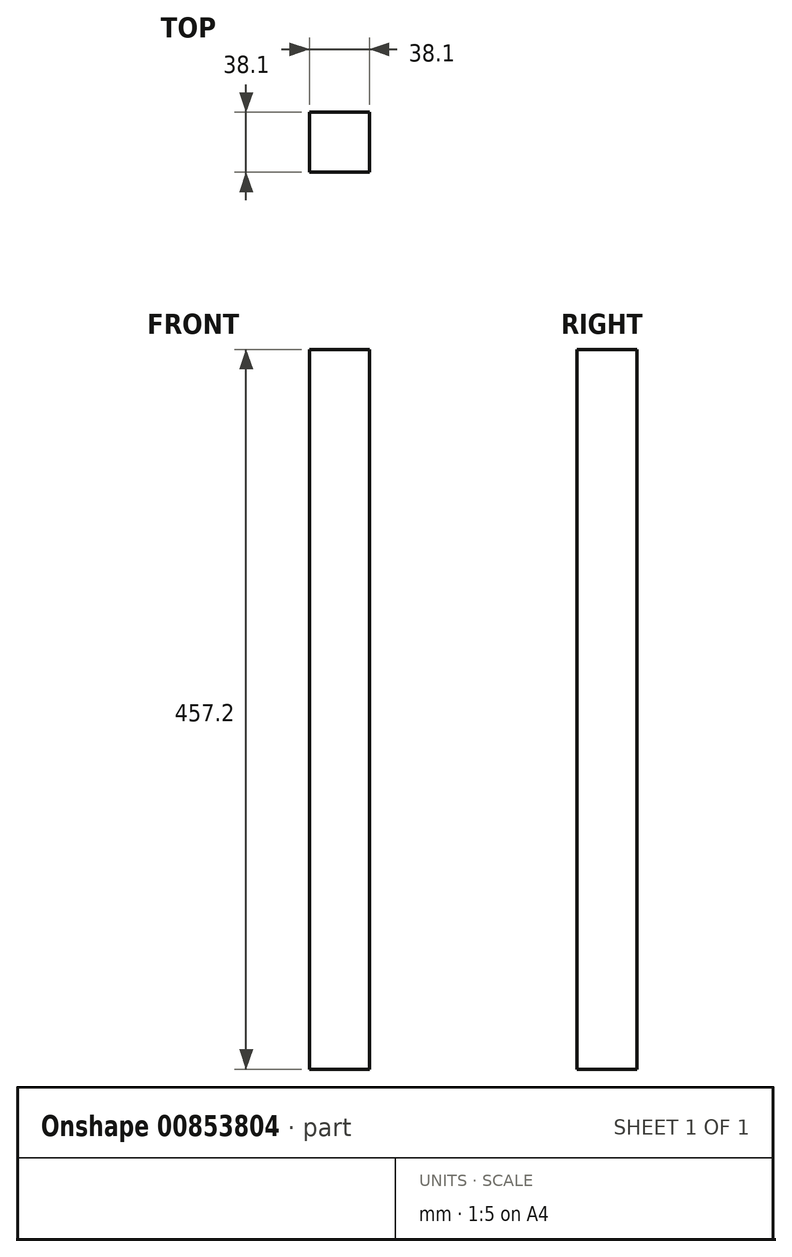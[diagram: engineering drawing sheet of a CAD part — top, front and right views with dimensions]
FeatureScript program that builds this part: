
annotation { "Feature Type Name" : "Feature", "Feature Type Description" : "" }
export const myFeature = defineFeature(function(context is Context, id is Id, definition is map)
    precondition{}
    {
        {
            var Q0;
            Q0=qCreatedBy(makeId("Top.planeOp"),FACE);
            var sketch = newSketch(context, id + "F0", { "sketchPlane" : qUnion([Q0])});
            skLineSegment(sketch, "E0.bottom", {"start": v(32.44, 13.16) * mm, "end": v(42.86, 13.16) * mm});
            skLineSegment(sketch, "E0.top", {"start": v(32.44, 12.64) * mm, "end": v(42.86, 12.64) * mm});
            skLineSegment(sketch, "E0.left", {"start": v(32.44, 13.16) * mm, "end": v(32.44, 12.64) * mm});
            skLineSegment(sketch, "E0.right", {"start": v(42.86, 13.16) * mm, "end": v(42.86, 12.64) * mm});
            skLineSegment(sketch, "E1.bottom", {"start": v(42.86, 12.64) * mm, "end": v(49.86, 12.64) * mm});
            skLineSegment(sketch, "E1.top", {"start": v(42.86, 5.15) * mm, "end": v(49.86, 5.15) * mm});
            skLineSegment(sketch, "E1.left", {"start": v(42.86, 12.64) * mm, "end": v(42.86, 5.15) * mm});
            skLineSegment(sketch, "E1.right", {"start": v(49.86, 12.64) * mm, "end": v(49.86, 5.15) * mm});
            skSolve(sketch);
        }
        {
            var Q0;
            Q0=makeQuery(id+"F0.imprint","IMPRINT",FACE,{"disambiguationData":[TD([[makeQuery(id+"F0.imprint","IMPRINT",EDGE,{"derivedFrom":sQuery(id+"F0.wireOp",EDGE,"E1.bottom")}),-1.0]])]});
            extrude(context, id + "F1", {"entities" : qUnion([Q0]), "depth" : 38.1 * mm, "offsetDistance" : 25.4 * mm});
        }
        {
            var Q0;
            Q0=qCreatedBy(makeId("Top.planeOp"),FACE);
            var sketch = newSketch(context, id + "F2", { "sketchPlane" : qUnion([Q0])});
            skLineSegment(sketch, "E2.bottom", {"start": v(-65.35, -26.25) * mm, "end": v(-27.25, -26.25) * mm});
            skLineSegment(sketch, "E2.top", {"start": v(-65.35, -64.35) * mm, "end": v(-27.25, -64.35) * mm});
            skLineSegment(sketch, "E2.left", {"start": v(-65.35, -26.25) * mm, "end": v(-65.35, -64.35) * mm});
            skLineSegment(sketch, "E2.right", {"start": v(-27.25, -26.25) * mm, "end": v(-27.25, -64.35) * mm});
            skSolve(sketch);
        }
        {
            var Q0;
            Q0=makeQuery(id+"F2.imprint","IMPRINT",FACE,{"disambiguationData":[TD([[makeQuery(id+"F2.imprint","IMPRINT",EDGE,{"derivedFrom":sQuery(id+"F2.wireOp",EDGE,"E2.bottom")}),-1.0]])]});
            extrude(context, id + "F3", {"entities" : qUnion([Q0]), "depth" : 457.2 * mm, "offsetDistance" : 25.4 * mm});
        }
        {
            var Q0;
            Q0=makeQuery(id+"F1.opExtrude","SWEPT_BODY",BODY,{"disambiguationData":[OSD([sQuery(id+"F0.wireOp",EDGE,"E1.bottom"),sQuery(id+"F0.wireOp",EDGE,"E1.top"),sQuery(id+"F0.wireOp",EDGE,"E1.left"),sQuery(id+"F0.wireOp",EDGE,"E1.right")])]});
            deleteBodies(context, id + "F4", {"entities" : qUnion([Q0])});
        }
    });
